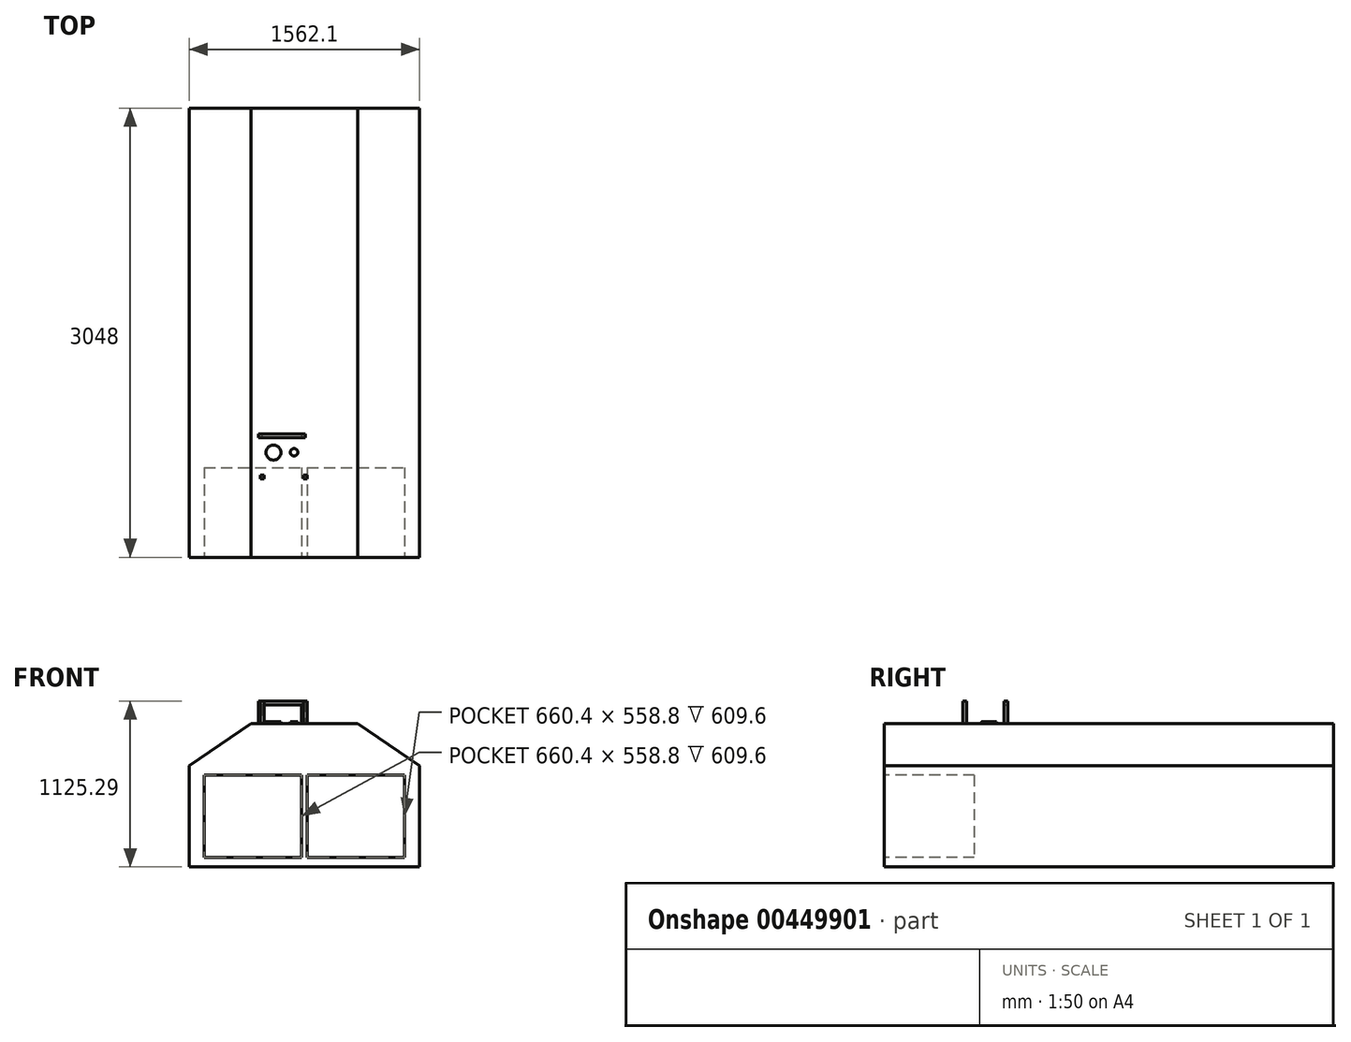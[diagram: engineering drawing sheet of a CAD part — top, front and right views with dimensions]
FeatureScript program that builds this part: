
annotation { "Feature Type Name" : "Feature", "Feature Type Description" : "" }
export const myFeature = defineFeature(function(context is Context, id is Id, definition is map)
    precondition{}
    {
        {
            var Q0;
            Q0=qCreatedBy(makeId("Front.planeOp"),FACE);
            var sketch = newSketch(context, id + "F0", { "sketchPlane" : qUnion([Q0])});
            skLineSegment(sketch, "E0", {"start": v(-1145.6, 166.8) * mm, "end": v(-1145.6, -519) * mm});
            skLineSegment(sketch, "E1", {"start": v(-1145.6, -519) * mm, "end": v(416.5, -519) * mm});
            skLineSegment(sketch, "E2", {"start": v(416.5, -519) * mm, "end": v(416.5, 166.8) * mm});
            skLineSegment(sketch, "E3", {"start": v(416.5, 166.8) * mm, "end": v(-2.6, 453.89) * mm});
            skLineSegment(sketch, "E4", {"start": v(-2.6, 453.89) * mm, "end": v(-726.5, 453.89) * mm});
            skLineSegment(sketch, "E5", {"start": v(-726.5, 453.89) * mm, "end": v(-1145.6, 166.8) * mm});
            skPoint(sketch, "E6.firstSnap0", {"position": v(-713.8, 103.3) * mm});
            skLineSegment(sketch, "E7", {"start": v(-1145.6, 166.8) * mm, "end": v(416.5, 166.8) * mm});
            skPoint(sketch, "E8.orphan", {"position": v(-1044, 103.3) * mm});
            skPoint(sketch, "E9.right.start.orphan", {"position": v(-383.6, 103.3) * mm});
            skPoint(sketch, "E6.top.end.orphan", {"position": v(-713.8, 103.3) * mm});
            skSolve(sketch);
        }
        {
            var Q0;
            Q0 = qSketchRegion(id + "F0", true);
            extrude(context, id + "F1", {"entities" : qUnion([Q0]), "depth" : 3048 * mm});
        }
        {
            var Q0;
            Q0=makeQuery(id+"F1.opExtrude","CAP_FACE",FACE,{"disambiguationData":[OSD([sQuery(id+"F0.wireOp",EDGE,"E0"),sQuery(id+"F0.wireOp",EDGE,"E1"),sQuery(id+"F0.wireOp",EDGE,"E2"),sQuery(id+"F0.wireOp",EDGE,"E3"),sQuery(id+"F0.wireOp",EDGE,"E4"),sQuery(id+"F0.wireOp",EDGE,"E5")])],"isStart":false});
            var sketch = newSketch(context, id + "F2", { "sketchPlane" : qUnion([Q0])});
            skLineSegment(sketch, "E10.bottom", {"start": v(-1044, 103.3) * mm, "end": v(-383.6, 103.3) * mm});
            skLineSegment(sketch, "E10.top", {"start": v(-1044, -455.5) * mm, "end": v(-383.6, -455.5) * mm});
            skLineSegment(sketch, "E10.left", {"start": v(-1044, 103.3) * mm, "end": v(-1044, -455.5) * mm});
            skLineSegment(sketch, "E10.right", {"start": v(-383.6, 103.3) * mm, "end": v(-383.6, -455.5) * mm});
            skLineSegment(sketch, "E11.bottom", {"start": v(-345.5, 103.3) * mm, "end": v(314.9, 103.3) * mm});
            skLineSegment(sketch, "E11.top", {"start": v(-345.5, -455.5) * mm, "end": v(314.9, -455.5) * mm});
            skLineSegment(sketch, "E11.left", {"start": v(-345.5, 103.3) * mm, "end": v(-345.5, -455.5) * mm});
            skLineSegment(sketch, "E11.right", {"start": v(314.9, 103.3) * mm, "end": v(314.9, -455.5) * mm});
            skSolve(sketch);
        }
        {
            var Q0;
            Q0 = qSketchRegion(id + "F2", true);
            extrude(context, id + "F3", {"entities" : qUnion([Q0]), "operationType" : NewBodyOperationType.REMOVE, "oppositeDirection" : true, "depth" : 609.6 * mm});
        }
        {
            var Q0;
            Q0=makeQuery(id+"F1.opExtrude","SWEPT_FACE",FACE,{"disambiguationData":[OSD([sQuery(id+"F0.wireOp",EDGE,"E4")])]});
            var sketch = newSketch(context, id + "F4", { "sketchPlane" : qUnion([Q0])});
            skCircle(sketch, "E12", {"center": v(-574.1, -2336.8) * mm, "radius": 50.8 * mm});
            skCircle(sketch, "E13", {"center": v(-434.4, -2334.9) * mm, "radius": 25.4 * mm});
            skSolve(sketch);
        }
        {
            var Q0;
            Q0 = qSketchRegion(id + "F4", true);
            extrude(context, id + "F5", {"entities" : qUnion([Q0]), "operationType" : NewBodyOperationType.ADD, "depth" : 12.7 * mm});
        }
        {
            var Q0;
            Q0=makeQuery(id+"F1.opExtrude","SWEPT_FACE",FACE,{"disambiguationData":[OSD([sQuery(id+"F0.wireOp",EDGE,"E4")])]});
            var sketch = newSketch(context, id + "F6", { "sketchPlane" : qUnion([Q0])});
            skLineSegment(sketch, "E14.bottom", {"start": v(-675.7, -2209.8) * mm, "end": v(-650.3, -2209.8) * mm});
            skLineSegment(sketch, "E14.top", {"start": v(-675.7, -2235.2) * mm, "end": v(-650.3, -2235.2) * mm});
            skLineSegment(sketch, "E14.left", {"start": v(-675.7, -2209.8) * mm, "end": v(-675.7, -2235.2) * mm});
            skLineSegment(sketch, "E14.right", {"start": v(-650.3, -2209.8) * mm, "end": v(-650.3, -2235.2) * mm});
            skPoint(sketch, "E14.middle", {"position": v(-663, -2222.5) * mm});
            skLineSegment(sketch, "E15.bottom", {"start": v(-383.6, -2209.8) * mm, "end": v(-358.2, -2209.8) * mm});
            skLineSegment(sketch, "E15.top", {"start": v(-383.6, -2235.2) * mm, "end": v(-358.2, -2235.2) * mm});
            skLineSegment(sketch, "E15.left", {"start": v(-383.6, -2209.8) * mm, "end": v(-383.6, -2235.2) * mm});
            skLineSegment(sketch, "E15.right", {"start": v(-358.2, -2209.8) * mm, "end": v(-358.2, -2235.2) * mm});
            skPoint(sketch, "E15.middle", {"position": v(-370.9, -2222.5) * mm});
            skLineSegment(sketch, "E16.bottom", {"start": v(-663, -2489.2) * mm, "end": v(-637.6, -2489.2) * mm});
            skLineSegment(sketch, "E16.top", {"start": v(-663, -2514.6) * mm, "end": v(-637.6, -2514.6) * mm});
            skLineSegment(sketch, "E16.left", {"start": v(-663, -2489.2) * mm, "end": v(-663, -2514.6) * mm});
            skLineSegment(sketch, "E16.right", {"start": v(-637.6, -2489.2) * mm, "end": v(-637.6, -2514.6) * mm});
            skPoint(sketch, "E16.middle", {"position": v(-650.3, -2501.9) * mm});
            skLineSegment(sketch, "E17.bottom", {"start": v(-370.9, -2489.2) * mm, "end": v(-345.5, -2489.2) * mm});
            skLineSegment(sketch, "E17.top", {"start": v(-370.9, -2514.6) * mm, "end": v(-345.5, -2514.6) * mm});
            skLineSegment(sketch, "E17.left", {"start": v(-370.9, -2489.2) * mm, "end": v(-370.9, -2514.6) * mm});
            skLineSegment(sketch, "E17.right", {"start": v(-345.5, -2489.2) * mm, "end": v(-345.5, -2514.6) * mm});
            skPoint(sketch, "E17.middle", {"position": v(-358.2, -2501.9) * mm});
            skSolve(sketch);
        }
        {
            var Q0;
            Q0 = qSketchRegion(id + "F6", true);
            extrude(context, id + "F7", {"entities" : qUnion([Q0]), "operationType" : NewBodyOperationType.ADD, "depth" : 152.4 * mm});
        }
        {
            var Q0;
            Q0=makeQuery(id+"F7.opExtrude","SWEPT_FACE",FACE,{"disambiguationData":[OSD([sQuery(id+"F6.wireOp",EDGE,"E14.right")])]});
            var sketch = newSketch(context, id + "F8", { "sketchPlane" : qUnion([Q0])});
            skLineSegment(sketch, "E18.bottom", {"start": v(-2235.2, 606.29) * mm, "end": v(-2209.8, 606.29) * mm});
            skLineSegment(sketch, "E18.top", {"start": v(-2235.2, 580.89) * mm, "end": v(-2209.8, 580.89) * mm});
            skLineSegment(sketch, "E18.left", {"start": v(-2235.2, 606.29) * mm, "end": v(-2235.2, 580.89) * mm});
            skLineSegment(sketch, "E18.right", {"start": v(-2209.8, 606.29) * mm, "end": v(-2209.8, 580.89) * mm});
            skSolve(sketch);
        }
        {
            var Q0;
            Q0=makeQuery(id+"F7.opExtrude","SWEPT_FACE",FACE,{"disambiguationData":[OSD([sQuery(id+"F6.wireOp",EDGE,"E15.left")])]});
            var sketch = newSketch(context, id + "F9", { "sketchPlane" : qUnion([Q0])});
            skLineSegment(sketch, "E19.bottom", {"start": v(2209.8, 606.29) * mm, "end": v(2235.2, 606.29) * mm});
            skLineSegment(sketch, "E19.top", {"start": v(2209.8, 580.89) * mm, "end": v(2235.2, 580.89) * mm});
            skLineSegment(sketch, "E19.left", {"start": v(2209.8, 606.29) * mm, "end": v(2209.8, 580.89) * mm});
            skLineSegment(sketch, "E19.right", {"start": v(2235.2, 606.29) * mm, "end": v(2235.2, 580.89) * mm});
            skSolve(sketch);
        }
        {
            var Q1;
            Q1=makeQuery(id+"F9.imprint","IMPRINT",FACE,{"disambiguationData":[TD([[makeQuery(id+"F9.imprint","IMPRINT",EDGE,{"derivedFrom":sQuery(id+"F9.wireOp",EDGE,"E19.bottom")}),-1.0]])]});
            var Q2;
            Q2=makeQuery(id+"F8.imprint","IMPRINT",FACE,{"disambiguationData":[TD([[makeQuery(id+"F8.imprint","IMPRINT",EDGE,{"derivedFrom":sQuery(id+"F8.wireOp",EDGE,"E18.bottom")}),1.0]])]});
            loft(context, id + "F10", {"operationType" : NewBodyOperationType.ADD, "sheetProfilesArray" : [{ "sheetProfileEntities" : qUnion([Q1]) }, { "sheetProfileEntities" : qUnion([Q2]) }]});
        }
    });
